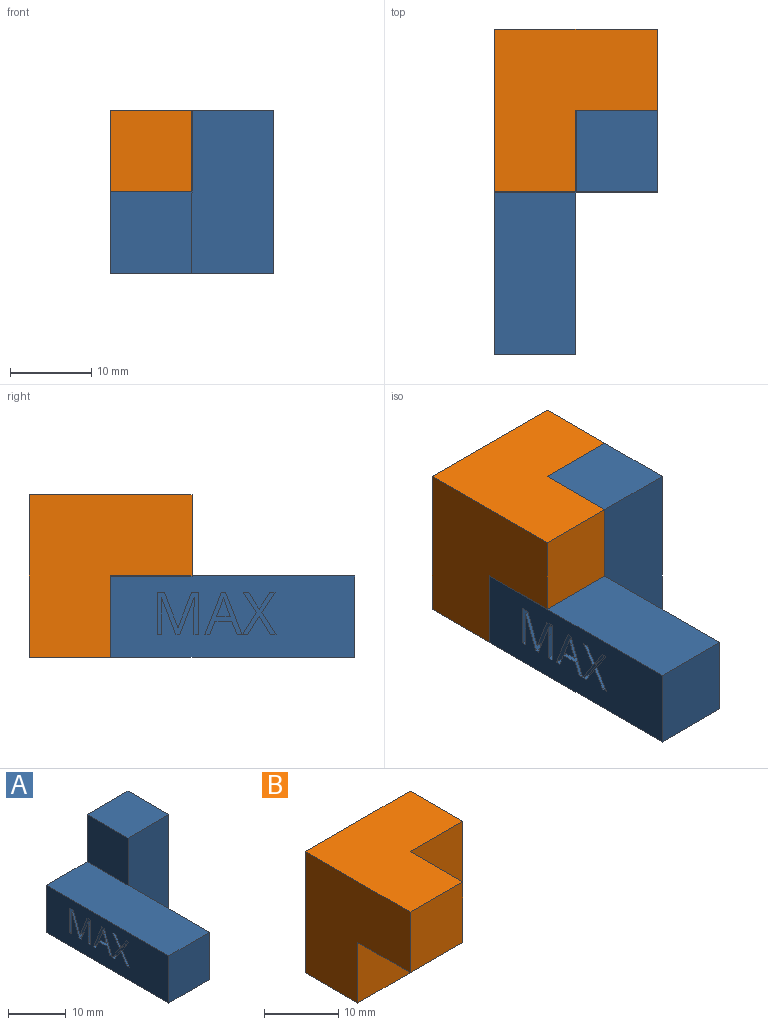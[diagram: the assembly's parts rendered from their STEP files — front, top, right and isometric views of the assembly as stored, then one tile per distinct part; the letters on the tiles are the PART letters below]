
ASSEMBLY  parts=2 mates=1
PART A: 57 faces, bbox 20x30x20 mm
  f0: plane 30x10mm, normal (-1,0,0), area 273.3mm2, adj f5,f6,f7,f9,f14,f15,f16,f17
  f1: plane 20x10mm, normal (0,-1,0), area 200mm2, adj f2,f3,f4,f6,f8
  f2: plane 10x10mm, normal (-1,0,0), area 100mm2, adj f1,f3,f5,f7
  f3: plane 10x10mm, normal (0,0,1), area 100mm2, adj f1,f2,f4,f5
  f4: plane 20x10mm, normal (1,0,0), area 200mm2, adj f1,f3,f5,f6
  f5: plane 20x20mm, normal (0,1,0), area 300mm2, adj f0,f2,f3,f4,f6,f7
  f6: plane 30x20mm, normal (0,0,-1), area 400mm2, adj f0,f1,f4,f5,f8,f9
  f7: plane 30x10mm, normal (0,0,1), area 300mm2, adj f0,f2,f5,f8,f9
  f8: plane 20x10mm, normal (1,0,0), area 200mm2, adj f1,f6,f7,f9
  f9: plane 10x10mm, normal (0,-1,0), area 100mm2, adj f0,f6,f7,f8
  f10: plane 1.61x1mm, normal (0,-0.94,0.35), area 1.7mm2, adj f11,f22,f23,f56
  f11: plane 1.68x1mm, normal (0,0,-1), area 1.7mm2, adj f10,f12,f23,f56
  f12: plane 1.61x1mm, normal (0,0.94,0.35), area 1.7mm2, adj f11,f13,f23,f56
  f13: extruded ~1x0.75mm, area 0.8mm2, adj f12,f22,f23,f56
  f14: plane 1.65x1mm, normal (0,-0.93,0.36), area 1.8mm2, adj f0,f15,f21,f23
  f15: plane 1x0.63mm, normal (0,0,1), area 0.6mm2, adj f0,f14,f16,f23
  f16: plane 5.22x2.04mm, normal (0,0.93,-0.36), area 5.6mm2, adj f0,f15,f17,f23
  f17: plane 1x0.51mm, normal (0,0,-1), area 0.5mm2, adj f0,f16,f18,f23
  f18: plane 5.22x2.05mm, normal (0,-0.93,-0.37), area 5.6mm2, adj f0,f17,f19,f23
  f19: plane 1x0.61mm, normal (0,0,1), area 0.6mm2, adj f0,f18,f20,f23
  f20: plane 1.65x1mm, normal (0,0.93,0.36), area 1.8mm2, adj f0,f19,f21,f23
  f21: plane 2.08x1mm, normal (0,0,1), area 2.1mm2, adj f0,f14,f20,f23
  f22: extruded ~1x0.75mm, area 0.8mm2, adj f10,f13,f23,f56
  f23: plane 5.22x4.61mm, normal (-1,0,0), area 6.9mm2, adj f10,f11,f12,f13,f14,f15,f16,f17
  f24: plane 1x0.69mm, normal (0,0,1), area 0.7mm2, adj f0,f25,f35,f36
  f25: plane 2.74x1.73mm, normal (0,0.84,-0.54), area 3.2mm2, adj f0,f24,f26,f36
  f26: plane 2.46x1.61mm, normal (0,0.84,0.55), area 2.9mm2, adj f0,f25,f27,f36
  f27: plane 1x0.64mm, normal (0,0,-1), area 0.6mm2, adj f0,f26,f28,f36
  f28: plane 2.06x1.3mm, normal (0,-0.85,-0.53), area 2.4mm2, adj f0,f27,f29,f36
  f29: plane 2.06x1.29mm, normal (0,0.85,-0.53), area 2.4mm2, adj f0,f28,f30,f36
  f30: plane 1x0.67mm, normal (0,0,-1), area 0.7mm2, adj f0,f29,f31,f36
  f31: plane 2.48x1.61mm, normal (0,-0.84,0.54), area 3mm2, adj f0,f30,f32,f36
  f32: plane 2.72x1.73mm, normal (0,-0.84,-0.54), area 3.2mm2, adj f0,f31,f33,f36
  f33: plane 1x0.64mm, normal (0,0,1), area 0.6mm2, adj f0,f32,f34,f36
  f34: plane 2.28x1.42mm, normal (0,0.85,0.53), area 2.7mm2, adj f0,f33,f35,f36
  f35: plane 2.28x1.4mm, normal (0,-0.85,0.52), area 2.7mm2, adj f0,f24,f34,f36
  f36: plane 5.2x4.14mm, normal (-1,0,0), area 6.4mm2, adj f24,f25,f26,f27,f28,f29,f30,f31
  f37: plane 4.61x1.76mm, normal (0,-0.93,0.36), area 4.9mm2, adj f0,f38,f54,f55
  f38: plane 1x0.49mm, normal (0,0,1), area 0.5mm2, adj f0,f37,f39,f55
  f39: plane 4.6x1.78mm, normal (0,0.93,0.36), area 4.9mm2, adj f0,f38,f40,f55
  f40: plane 1x0.03mm, normal (0,0,1), area 0mm2, adj f0,f39,f41,f55
  f41: extruded ~1.25x1mm, area 1.3mm2, adj f0,f40,f42,f55
  f42: plane 3.35x1mm, normal (0,-1,0), area 3.3mm2, adj f0,f41,f43,f55
  f43: plane 1x0.6mm, normal (0,0,1), area 0.6mm2, adj f0,f42,f44,f55
  f44: plane 5.2x1mm, normal (0,1,0), area 5.2mm2, adj f0,f43,f45,f55
  f45: plane 1x0.9mm, normal (0,0,-1), area 0.9mm2, adj f0,f44,f46,f55
  f46: plane 4.29x1.66mm, normal (0,-0.93,-0.36), area 4.6mm2, adj f0,f45,f47,f55
  f47: plane 1x0.03mm, normal (0,0,-1), area 0mm2, adj f0,f46,f48,f55
  f48: plane 4.29x1.65mm, normal (0,0.93,-0.36), area 4.6mm2, adj f0,f47,f49,f55
  f49: plane 1x0.91mm, normal (0,0,-1), area 0.9mm2, adj f0,f48,f50,f55
  f50: plane 5.2x1mm, normal (0,-1,0), area 5.2mm2, adj f0,f49,f51,f55
  f51: plane 1x0.56mm, normal (0,0,1), area 0.6mm2, adj f0,f50,f52,f55
  f52: plane 3.3x1mm, normal (0,1,0), area 3.3mm2, adj f0,f51,f53,f55
  f53: extruded ~1.3x1mm, area 1.3mm2, adj f0,f52,f54,f55
  f54: plane 1x0.03mm, normal (0,0,1), area 0mm2, adj f0,f37,f53,f55
  f55: plane 5.2x5.15mm, normal (-1,0,0), area 11.5mm2, adj f37,f38,f39,f40,f41,f42,f43,f44
  f56: plane 2.36x1.68mm, normal (-1,0,0), area 1.9mm2, adj f10,f11,f12,f13,f22
PART B: 12 faces, bbox 20x20x20 mm
  f0: plane 10x10mm, normal (0,0,-1), area 100mm2, adj f6,f7,f8,f9
  f1: plane 20x20mm, normal (0,0,1), area 300mm2, adj f2,f4,f5,f6,f7,f8
  f2: plane 20x20mm, normal (-1,0,0), area 300mm2, adj f1,f3,f5,f6,f10,f11
  f3: plane 10x10mm, normal (0,0,-1), area 100mm2, adj f2,f4,f5,f10
  f4: plane 10x10mm, normal (1,0,0), area 100mm2, adj f1,f3,f5,f7
  f5: plane 10x10mm, normal (0,-1,0), area 100mm2, adj f1,f2,f3,f4
  f6: plane 20x20mm, normal (0,1,0), area 300mm2, adj f0,f1,f2,f8,f9,f11
  f7: plane 10x10mm, normal (0,-1,0), area 100mm2, adj f0,f1,f4,f8
  f8: plane 10x10mm, normal (1,0,0), area 100mm2, adj f0,f1,f6,f7
  f9: plane 10x10mm, normal (1,0,0), area 100mm2, adj f0,f6,f10,f11
  f10: plane 10x10mm, normal (0,-1,0), area 100mm2, adj f2,f3,f9,f11
  f11: plane 10x10mm, normal (0,0,-1), area 100mm2, adj f2,f6,f9,f10
PLACE A t=(-7.97,-10.27,-1.96)mm
PLACE B t=(5.86,-0.27,-13.33)mm
MATE fastened A.f2 <-> B.f4  axis (-1,0,0) through (-37.03,-20.27,23.95)mm
